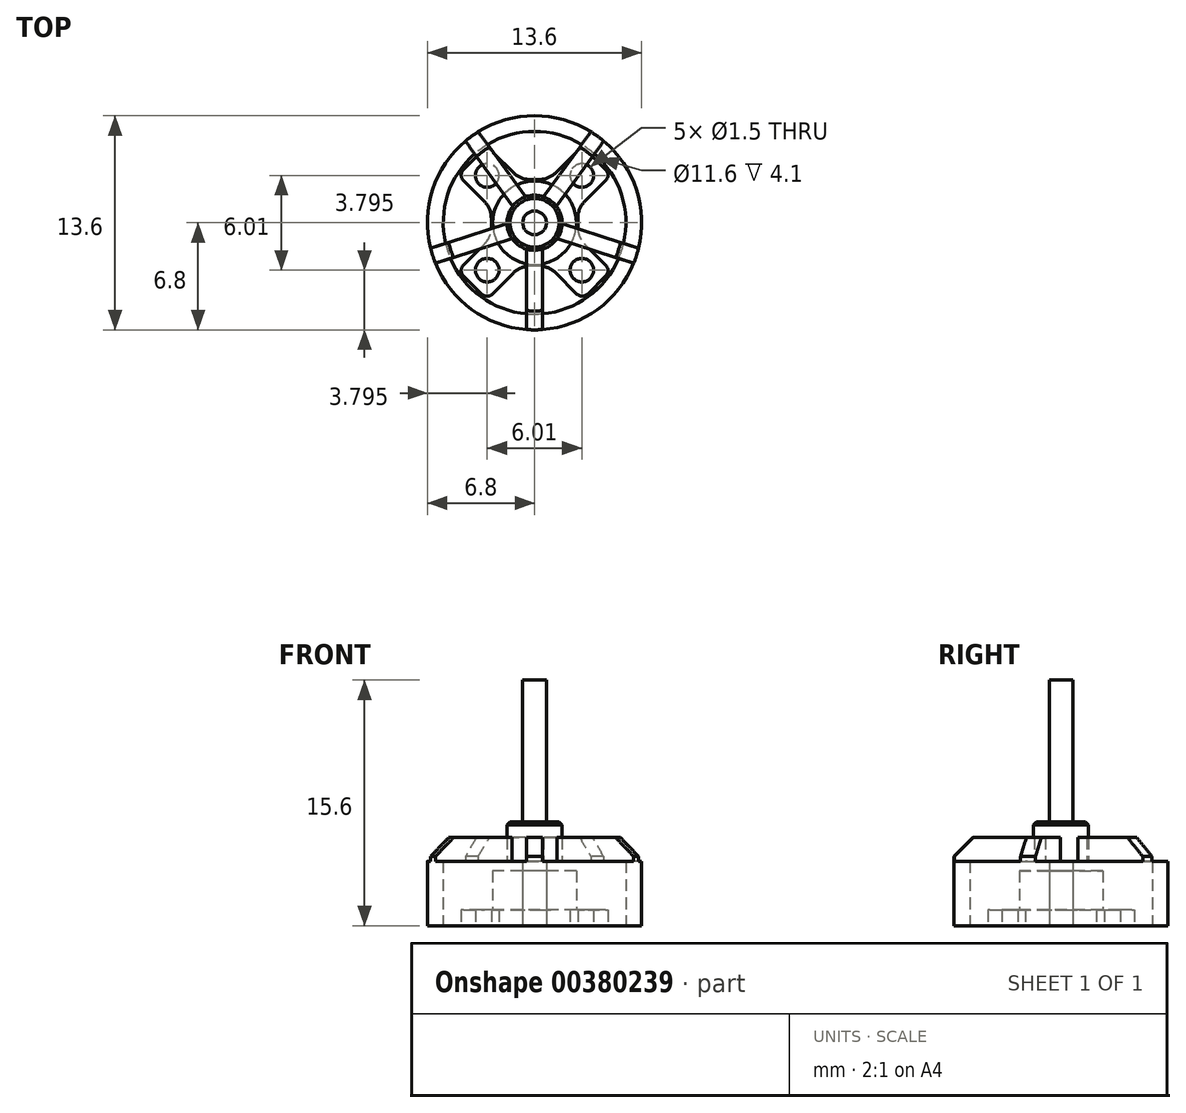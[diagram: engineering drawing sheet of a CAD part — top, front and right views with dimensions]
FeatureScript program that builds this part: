
annotation { "Feature Type Name" : "Feature", "Feature Type Description" : "" }
export const myFeature = defineFeature(function(context is Context, id is Id, definition is map)
    precondition{}
    {
        {
            var Q0;
            Q0=qCreatedBy(makeId("Top.planeOp"),FACE);
            var sketch = newSketch(context, id + "F0", { "sketchPlane" : qUnion([Q0])});
            skCircle(sketch, "E0", {"center": v(0, 0) * mm, "radius": 4.25 * mm, "construction": true});
            skLineSegment(sketch, "E1", {"start": v(-7.64, 0) * mm, "end": v(7.53, 0) * mm, "construction": true});
            skLineSegment(sketch, "E2", {"start": v(0, 0) * mm, "end": v(-7.7, 7.7) * mm, "construction": true});
            skLineSegment(sketch, "E3", {"start": v(0, 0) * mm, "end": v(5.02, -5.02) * mm, "construction": true});
            skLineSegment(sketch, "E4", {"start": v(0, 0) * mm, "end": v(-5.33, -5.33) * mm, "construction": true});
            skLineSegment(sketch, "E5", {"start": v(0, 0) * mm, "end": v(4.89, 4.89) * mm, "construction": true});
            skCircle(sketch, "E6", {"center": v(-3, 3) * mm, "radius": 0.75 * mm});
            skCircle(sketch, "E7", {"center": v(3, 3) * mm, "radius": 0.75 * mm});
            skCircle(sketch, "E8", {"center": v(3, -3) * mm, "radius": 0.75 * mm});
            skCircle(sketch, "E9", {"center": v(-3, -3) * mm, "radius": 0.75 * mm});
            skLineSegment(sketch, "E10", {"start": v(3.38, 4.51) * mm, "end": v(4.51, 3.38) * mm});
            skCircle(sketch, "E11", {"center": v(0, 0) * mm, "radius": 1.74 * mm, "construction": true});
            skLineSegment(sketch, "E12", {"start": v(2.68, 4.51) * mm, "end": v(1.35, 3.19) * mm});
            skLineSegment(sketch, "E13", {"start": v(4.51, 2.68) * mm, "end": v(3.19, 1.35) * mm});
            skPoint(sketch, "E14.visualSharp", {"position": v(3.03, 4.87) * mm});
            skArc(sketch, "E14.filletArc", {"start": v(3.38, 4.51) * mm, "mid": v(3.03, 4.66) * mm, "end": v(2.68, 4.51) * mm});
            skPoint(sketch, "E15.visualSharp", {"position": v(4.87, 3.03) * mm});
            skArc(sketch, "E15.filletArc", {"start": v(4.51, 2.68) * mm, "mid": v(4.66, 3.03) * mm, "end": v(4.51, 3.38) * mm});
            skLineSegment(sketch, "E16", {"start": v(0, 5.01) * mm, "end": v(0, -5.05) * mm, "construction": true});
            skLineSegment(sketch, "E17.MirrorCS", {"start": v(-2.68, 4.51) * mm, "end": v(-1.35, 3.19) * mm});
            skArc(sketch, "E18.MirrorCS", {"start": v(-3.38, 4.51) * mm, "mid": v(-3.03, 4.66) * mm, "end": v(-2.68, 4.51) * mm});
            skLineSegment(sketch, "E19.MirrorCS", {"start": v(-3.38, 4.51) * mm, "end": v(-4.51, 3.38) * mm});
            skLineSegment(sketch, "E20.MirrorCS", {"start": v(-4.51, 2.68) * mm, "end": v(-3.19, 1.35) * mm});
            skArc(sketch, "E21.MirrorCS", {"start": v(-4.51, 2.68) * mm, "mid": v(-4.66, 3.03) * mm, "end": v(-4.51, 3.38) * mm});
            skLineSegment(sketch, "E22.MirrorCS", {"start": v(-4.51, -2.68) * mm, "end": v(-3.19, -1.35) * mm});
            skArc(sketch, "E23.MirrorCS", {"start": v(-4.51, -2.68) * mm, "mid": v(-4.66, -3.03) * mm, "end": v(-4.51, -3.38) * mm});
            skLineSegment(sketch, "E24.MirrorCS", {"start": v(-3.38, -4.51) * mm, "end": v(-4.51, -3.38) * mm});
            skArc(sketch, "E25.MirrorCS", {"start": v(-3.38, -4.51) * mm, "mid": v(-3.03, -4.66) * mm, "end": v(-2.68, -4.51) * mm});
            skLineSegment(sketch, "E26.MirrorCS", {"start": v(-2.68, -4.51) * mm, "end": v(-1.35, -3.19) * mm});
            skLineSegment(sketch, "E27.MirrorCS", {"start": v(2.68, -4.51) * mm, "end": v(1.35, -3.19) * mm});
            skArc(sketch, "E28.MirrorCS", {"start": v(3.38, -4.51) * mm, "mid": v(3.03, -4.66) * mm, "end": v(2.68, -4.51) * mm});
            skLineSegment(sketch, "E29.MirrorCS", {"start": v(3.38, -4.51) * mm, "end": v(4.51, -3.38) * mm});
            skArc(sketch, "E30.MirrorCS", {"start": v(4.51, -2.68) * mm, "mid": v(4.66, -3.03) * mm, "end": v(4.51, -3.38) * mm});
            skLineSegment(sketch, "E31.MirrorCS", {"start": v(4.51, -2.68) * mm, "end": v(3.19, -1.35) * mm});
            skLineSegment(sketch, "E32", {"start": v(-0.29, 2.75) * mm, "end": v(0.29, 2.75) * mm});
            skLineSegment(sketch, "E33", {"start": v(2.75, 0.29) * mm, "end": v(2.75, -0.29) * mm});
            skLineSegment(sketch, "E34", {"start": v(0.29, -2.75) * mm, "end": v(-0.29, -2.75) * mm});
            skLineSegment(sketch, "E35", {"start": v(-2.75, -0.29) * mm, "end": v(-2.75, 0.29) * mm});
            skPoint(sketch, "E36.visualSharp", {"position": v(-0.9, 2.75) * mm});
            skArc(sketch, "E36.filletArc", {"start": v(-1.35, 3.19) * mm, "mid": v(-0.86, 2.86) * mm, "end": v(-0.29, 2.75) * mm});
            skPoint(sketch, "E37.visualSharp", {"position": v(0.9, 2.75) * mm});
            skArc(sketch, "E37.filletArc", {"start": v(0.29, 2.75) * mm, "mid": v(0.86, 2.86) * mm, "end": v(1.35, 3.19) * mm});
            skPoint(sketch, "E38.visualSharp", {"position": v(-2.75, -0.9) * mm});
            skArc(sketch, "E38.filletArc", {"start": v(-3.19, -1.35) * mm, "mid": v(-2.86, -0.86) * mm, "end": v(-2.75, -0.29) * mm});
            skPoint(sketch, "E39.visualSharp", {"position": v(-2.75, 0.9) * mm});
            skArc(sketch, "E39.filletArc", {"start": v(-2.75, 0.29) * mm, "mid": v(-2.86, 0.86) * mm, "end": v(-3.19, 1.35) * mm});
            skPoint(sketch, "E40.visualSharp", {"position": v(2.75, 0.9) * mm});
            skArc(sketch, "E40.filletArc", {"start": v(3.19, 1.35) * mm, "mid": v(2.86, 0.86) * mm, "end": v(2.75, 0.29) * mm});
            skPoint(sketch, "E41.visualSharp", {"position": v(2.75, -0.9) * mm});
            skArc(sketch, "E41.filletArc", {"start": v(2.75, -0.29) * mm, "mid": v(2.86, -0.86) * mm, "end": v(3.19, -1.35) * mm});
            skPoint(sketch, "E42.visualSharp", {"position": v(0.9, -2.75) * mm});
            skArc(sketch, "E42.filletArc", {"start": v(1.35, -3.19) * mm, "mid": v(0.86, -2.86) * mm, "end": v(0.29, -2.75) * mm});
            skPoint(sketch, "E43.visualSharp", {"position": v(-0.9, -2.75) * mm});
            skArc(sketch, "E43.filletArc", {"start": v(-0.29, -2.75) * mm, "mid": v(-0.86, -2.86) * mm, "end": v(-1.35, -3.19) * mm});
            skCircle(sketch, "E44", {"center": v(0, 0) * mm, "radius": 0.75 * mm});
            skSolve(sketch);
        }
        {
            var Q0;
            Q0=makeQuery(id+"F0.imprint","IMPRINT",FACE,{"disambiguationData":[TD([[makeQuery(id+"F0.imprint","IMPRINT",EDGE,{"derivedFrom":sQuery(id+"F0.wireOp",EDGE,"E6")}),-1.0]])]});
            extrude(context, id + "F1", {"entities" : qUnion([Q0]), "depth" : 1 * mm});
        }
        {
            var Q0;
            Q0=qCreatedBy(makeId("Top.planeOp"),FACE);
            var sketch = newSketch(context, id + "F2", { "sketchPlane" : qUnion([Q0])});
            skCircle(sketch, "E45", {"center": v(0, 0) * mm, "radius": 6.8 * mm});
            skCircle(sketch, "E46", {"center": v(0, 0) * mm, "radius": 5.8 * mm});
            skSolve(sketch);
        }
        {
            var Q0;
            Q0=makeQuery(id+"F2.imprint","IMPRINT",FACE,{"disambiguationData":[TD([[makeQuery(id+"F2.imprint","IMPRINT",EDGE,{"derivedFrom":sQuery(id+"F2.wireOp",EDGE,"E45")}),1.0]])]});
            extrude(context, id + "F3", {"entities" : qUnion([Q0]), "depth" : 4.1 * mm});
        }
        {
            var Q0;
            Q0=makeQuery(id+"F1.opExtrude","CAP_FACE",FACE,{"disambiguationData":[OSD([sQuery(id+"F0.wireOp",EDGE,"E6"),sQuery(id+"F0.wireOp",EDGE,"E7"),sQuery(id+"F0.wireOp",EDGE,"E8"),sQuery(id+"F0.wireOp",EDGE,"E9"),sQuery(id+"F0.wireOp",EDGE,"E10"),sQuery(id+"F0.wireOp",EDGE,"E12"),sQuery(id+"F0.wireOp",EDGE,"E13"),sQuery(id+"F0.wireOp",EDGE,"E14.filletArc"),sQuery(id+"F0.wireOp",EDGE,"E15.filletArc"),sQuery(id+"F0.wireOp",EDGE,"E17.MirrorCS"),sQuery(id+"F0.wireOp",EDGE,"E18.MirrorCS"),sQuery(id+"F0.wireOp",EDGE,"E19.MirrorCS"),sQuery(id+"F0.wireOp",EDGE,"E20.MirrorCS"),sQuery(id+"F0.wireOp",EDGE,"E21.MirrorCS"),sQuery(id+"F0.wireOp",EDGE,"E22.MirrorCS"),sQuery(id+"F0.wireOp",EDGE,"E23.MirrorCS"),sQuery(id+"F0.wireOp",EDGE,"E24.MirrorCS"),sQuery(id+"F0.wireOp",EDGE,"E25.MirrorCS"),sQuery(id+"F0.wireOp",EDGE,"E26.MirrorCS"),sQuery(id+"F0.wireOp",EDGE,"E27.MirrorCS"),sQuery(id+"F0.wireOp",EDGE,"E28.MirrorCS"),sQuery(id+"F0.wireOp",EDGE,"E29.MirrorCS"),sQuery(id+"F0.wireOp",EDGE,"E30.MirrorCS"),sQuery(id+"F0.wireOp",EDGE,"E31.MirrorCS"),sQuery(id+"F0.wireOp",EDGE,"E32"),sQuery(id+"F0.wireOp",EDGE,"E33"),sQuery(id+"F0.wireOp",EDGE,"E34"),sQuery(id+"F0.wireOp",EDGE,"E35"),sQuery(id+"F0.wireOp",EDGE,"E36.filletArc"),sQuery(id+"F0.wireOp",EDGE,"E37.filletArc"),sQuery(id+"F0.wireOp",EDGE,"E38.filletArc"),sQuery(id+"F0.wireOp",EDGE,"E39.filletArc"),sQuery(id+"F0.wireOp",EDGE,"E40.filletArc"),sQuery(id+"F0.wireOp",EDGE,"E41.filletArc"),sQuery(id+"F0.wireOp",EDGE,"E42.filletArc"),sQuery(id+"F0.wireOp",EDGE,"E43.filletArc")])],"isStart":false});
            var sketch = newSketch(context, id + "F4", { "sketchPlane" : qUnion([Q0])});
            skCircle(sketch, "E47", {"center": v(0, 0) * mm, "radius": 2.66 * mm});
            skSolve(sketch);
        }
        {
            var Q0;
            Q0=makeQuery(id+"F4.imprint","IMPRINT",FACE,{"disambiguationData":[TD([[makeQuery(id+"F4.imprint","IMPRINT",EDGE,{"derivedFrom":sQuery(id+"F4.wireOp",EDGE,"E47")}),1.0]])]});
            extrude(context, id + "F5", {"entities" : qUnion([Q0]), "operationType" : NewBodyOperationType.ADD, "depth" : 2.5 * mm});
        }
        {
            var Q0;
            Q0=makeQuery(id+"F3.opExtrude","CAP_FACE",FACE,{"disambiguationData":[OSD([sQuery(id+"F2.wireOp",EDGE,"E45"),sQuery(id+"F2.wireOp",EDGE,"E46")])],"isStart":false});
            var sketch = newSketch(context, id + "F6", { "sketchPlane" : qUnion([Q0])});
            skLineSegment(sketch, "E48", {"start": v(0, -8.68) * mm, "end": v(0, 0) * mm, "construction": true});
            skLineSegment(sketch, "E49", {"start": v(0, 0) * mm, "end": v(-6.56, 9.02) * mm, "construction": true});
            skLineSegment(sketch, "E50", {"start": v(0, 0) * mm, "end": v(5.24, 7.22) * mm, "construction": true});
            skLineSegment(sketch, "E51", {"start": v(0, 0) * mm, "end": v(8.23, -2.67) * mm, "construction": true});
            skCircle(sketch, "E52", {"center": v(0, 0) * mm, "radius": 1.75 * mm});
            skCircle(sketch, "E53", {"center": v(0, 0) * mm, "radius": 0.75 * mm});
            skLineSegment(sketch, "E54", {"start": v(-1.66, -0.54) * mm, "end": v(-6.47, -2.1) * mm, "construction": true});
            skLineSegment(sketch, "E55", {"start": v(-4.07, -1.32) * mm, "end": v(-4.22, -0.85) * mm, "construction": true});
            skLineSegment(sketch, "E56", {"start": v(-4.22, -0.85) * mm, "end": v(-6.6, -1.62) * mm});
            skLineSegment(sketch, "E57", {"start": v(-4.22, -0.85) * mm, "end": v(-1.75, -0.04) * mm});
            skLineSegment(sketch, "E58", {"start": v(-4.07, -1.32) * mm, "end": v(-3.91, -1.8) * mm, "construction": true});
            skLineSegment(sketch, "E59", {"start": v(-3.91, -1.8) * mm, "end": v(-6.3, -2.57) * mm});
            skLineSegment(sketch, "E60", {"start": v(-3.91, -1.8) * mm, "end": v(-1.44, -1) * mm});
            skLineSegment(sketch, "E61.1.0", {"start": v(-0.5, -4.27) * mm, "end": v(-0.5, -6.78) * mm});
            skLineSegment(sketch, "E61.1.1", {"start": v(-0.5, -4.27) * mm, "end": v(-0.5, -1.68) * mm});
            skLineSegment(sketch, "E61.1.2", {"start": v(0.5, -4.28) * mm, "end": v(0.5, -1.68) * mm});
            skLineSegment(sketch, "E61.1.3", {"start": v(0.5, -4.27) * mm, "end": v(0.5, -6.78) * mm});
            skLineSegment(sketch, "E61.2.0", {"start": v(3.91, -1.8) * mm, "end": v(6.3, -2.57) * mm});
            skLineSegment(sketch, "E61.2.1", {"start": v(3.91, -1.8) * mm, "end": v(1.44, -1) * mm});
            skLineSegment(sketch, "E61.2.2", {"start": v(4.22, -0.85) * mm, "end": v(1.75, -0.04) * mm});
            skLineSegment(sketch, "E61.2.3", {"start": v(4.22, -0.85) * mm, "end": v(6.6, -1.62) * mm});
            skLineSegment(sketch, "E61.3.0", {"start": v(2.92, 3.16) * mm, "end": v(4.4, 5.2) * mm});
            skLineSegment(sketch, "E61.3.1", {"start": v(2.92, 3.16) * mm, "end": v(1.4, 1.06) * mm});
            skLineSegment(sketch, "E61.3.2", {"start": v(2.1, 3.75) * mm, "end": v(0.58, 1.65) * mm});
            skLineSegment(sketch, "E61.3.3", {"start": v(2.1, 3.75) * mm, "end": v(3.58, 5.78) * mm});
            skLineSegment(sketch, "E61.4.0", {"start": v(-2.1, 3.75) * mm, "end": v(-3.58, 5.78) * mm});
            skLineSegment(sketch, "E61.4.1", {"start": v(-2.1, 3.75) * mm, "end": v(-0.58, 1.65) * mm});
            skLineSegment(sketch, "E61.4.2", {"start": v(-2.92, 3.16) * mm, "end": v(-1.4, 1.06) * mm});
            skLineSegment(sketch, "E61.4.3", {"start": v(-2.92, 3.16) * mm, "end": v(-4.4, 5.2) * mm});
            skSolve(sketch);
        }
        {
            var Q0;
            {var subQ6=sQuery(id+"F6.wireOp",EDGE,"E61.4.1");Q0=makeQuery(id+"F6.imprint","IMPRINT",FACE,{"disambiguationData":[TD([[makeQuery(id+"F6.imprint","IMPRINT",EDGE,{"derivedFrom":subQ6}),-1.0]])]});}
            var Q1;
            {var subQ0=sQuery(id+"F6.wireOp",EDGE,"E61.4.0");var subQ1=makeQuery(id+"F3.opExtrude","CAP_EDGE",EDGE,{"disambiguationData":[OSD([sQuery(id+"F2.wireOp",EDGE,"E45")])],"isStart":false});var subQ2=makeQuery(id+"F6.imprint","INTERSECT",VERTEX,{"derivedFrom":[subQ1,subQ0]});Q1=makeQuery(id+"F6.imprint","IMPRINT",FACE,{"disambiguationData":[TD([[makeQuery(id+"F6.imprint","IMPRINT",EDGE,{"disambiguationData":[TD([[subQ2,1.0]])],"derivedFrom":subQ0}),1.0]])]});}
            var Q2;
            {var subQ1=sQuery(id+"F6.wireOp",EDGE,"E61.3.1");Q2=makeQuery(id+"F6.imprint","IMPRINT",FACE,{"disambiguationData":[TD([[makeQuery(id+"F6.imprint","IMPRINT",EDGE,{"derivedFrom":subQ1}),-1.0]])]});}
            var Q3;
            {var subQ0=sQuery(id+"F6.wireOp",EDGE,"E61.3.0");var subQ1=makeQuery(id+"F3.opExtrude","CAP_EDGE",EDGE,{"disambiguationData":[OSD([sQuery(id+"F2.wireOp",EDGE,"E45")])],"isStart":false});var subQ2=makeQuery(id+"F6.imprint","INTERSECT",VERTEX,{"derivedFrom":[subQ1,subQ0]});Q3=makeQuery(id+"F6.imprint","IMPRINT",FACE,{"disambiguationData":[TD([[makeQuery(id+"F6.imprint","IMPRINT",EDGE,{"disambiguationData":[TD([[subQ2,1.0]])],"derivedFrom":subQ0}),1.0]])]});}
            var Q4;
            {var subQ1=sQuery(id+"F6.wireOp",EDGE,"E61.2.1");Q4=makeQuery(id+"F6.imprint","IMPRINT",FACE,{"disambiguationData":[TD([[makeQuery(id+"F6.imprint","IMPRINT",EDGE,{"derivedFrom":subQ1}),-1.0]])]});}
            var Q5;
            {var subQ0=sQuery(id+"F6.wireOp",EDGE,"E61.2.0");var subQ1=makeQuery(id+"F3.opExtrude","CAP_EDGE",EDGE,{"disambiguationData":[OSD([sQuery(id+"F2.wireOp",EDGE,"E45")])],"isStart":false});var subQ2=makeQuery(id+"F6.imprint","INTERSECT",VERTEX,{"derivedFrom":[subQ1,subQ0]});Q5=makeQuery(id+"F6.imprint","IMPRINT",FACE,{"disambiguationData":[TD([[makeQuery(id+"F6.imprint","IMPRINT",EDGE,{"disambiguationData":[TD([[subQ2,1.0]])],"derivedFrom":subQ0}),1.0]])]});}
            var Q6;
            {var subQ1=sQuery(id+"F6.wireOp",EDGE,"E61.1.1");Q6=makeQuery(id+"F6.imprint","IMPRINT",FACE,{"disambiguationData":[TD([[makeQuery(id+"F6.imprint","IMPRINT",EDGE,{"derivedFrom":subQ1}),-1.0]])]});}
            var Q7;
            {var subQ0=sQuery(id+"F6.wireOp",EDGE,"E57");Q7=makeQuery(id+"F6.imprint","IMPRINT",FACE,{"disambiguationData":[TD([[makeQuery(id+"F6.imprint","IMPRINT",EDGE,{"derivedFrom":subQ0}),-1.0]])]});}
            var Q8;
            {var subQ0=sQuery(id+"F6.wireOp",EDGE,"E56");var subQ1=makeQuery(id+"F3.opExtrude","CAP_EDGE",EDGE,{"disambiguationData":[OSD([sQuery(id+"F2.wireOp",EDGE,"E45")])],"isStart":false});var subQ2=makeQuery(id+"F6.imprint","INTERSECT",VERTEX,{"derivedFrom":[subQ1,subQ0]});Q8=makeQuery(id+"F6.imprint","IMPRINT",FACE,{"disambiguationData":[TD([[makeQuery(id+"F6.imprint","IMPRINT",EDGE,{"disambiguationData":[TD([[subQ2,1.0]])],"derivedFrom":subQ0}),1.0]])]});}
            var Q9;
            Q9=makeQuery(id+"F6.imprint","IMPRINT",FACE,{"disambiguationData":[TD([[makeQuery(id+"F6.imprint","IMPRINT",EDGE,{"derivedFrom":sQuery(id+"F6.wireOp",EDGE,"E53")}),-1.0]])]});
            var Q10;
            {var subQ0=sQuery(id+"F6.wireOp",EDGE,"E61.1.0");var subQ1=makeQuery(id+"F3.opExtrude","CAP_EDGE",EDGE,{"disambiguationData":[OSD([sQuery(id+"F2.wireOp",EDGE,"E45")])],"isStart":false});var subQ2=makeQuery(id+"F6.imprint","INTERSECT",VERTEX,{"derivedFrom":[subQ1,subQ0]});Q10=makeQuery(id+"F6.imprint","IMPRINT",FACE,{"disambiguationData":[TD([[makeQuery(id+"F6.imprint","IMPRINT",EDGE,{"disambiguationData":[TD([[subQ2,1.0]])],"derivedFrom":subQ0}),1.0]])]});}
            extrude(context, id + "F7", {"entities" : qUnion([Q0, Q1, Q2, Q3, Q4, Q5, Q6, Q7, Q8, Q9, Q10]), "operationType" : NewBodyOperationType.ADD, "depth" : 1.5 * mm});
        }
        {
            var Q0;
            {var subQ0=sQuery(id+"F2.wireOp",EDGE,"E45");var subQ1=makeQuery(id+"F3.opExtrude","CAP_EDGE",EDGE,{"disambiguationData":[OSD([subQ0])],"isStart":false});Q0=makeQuery(id+"F7.opExtrude","CAP_EDGE",EDGE,{"disambiguationData":[OSD([subQ0]),TDD([makeQuery(id+"F6.imprint","IMPRINT",EDGE,{"disambiguationData":[TD([[makeQuery(id+"F6.imprint","INTERSECT",VERTEX,{"derivedFrom":[subQ1,sQuery(id+"F6.wireOp",EDGE,"E56")]}),-1.0]])],"derivedFrom":subQ1})])],"isStart":false});}
            var Q1;
            {var subQ0=sQuery(id+"F2.wireOp",EDGE,"E45");var subQ1=makeQuery(id+"F3.opExtrude","CAP_EDGE",EDGE,{"disambiguationData":[OSD([subQ0])],"isStart":false});Q1=makeQuery(id+"F7.opExtrude","CAP_EDGE",EDGE,{"disambiguationData":[OSD([subQ0]),TDD([makeQuery(id+"F6.imprint","IMPRINT",EDGE,{"disambiguationData":[TD([[makeQuery(id+"F6.imprint","INTERSECT",VERTEX,{"derivedFrom":[subQ1,sQuery(id+"F6.wireOp",EDGE,"E61.4.0")]}),-1.0]])],"derivedFrom":subQ1})])],"isStart":false});}
            var Q2;
            {var subQ0=sQuery(id+"F2.wireOp",EDGE,"E45");var subQ1=makeQuery(id+"F3.opExtrude","CAP_EDGE",EDGE,{"disambiguationData":[OSD([subQ0])],"isStart":false});Q2=makeQuery(id+"F7.opExtrude","CAP_EDGE",EDGE,{"disambiguationData":[OSD([subQ0]),TDD([makeQuery(id+"F6.imprint","IMPRINT",EDGE,{"disambiguationData":[TD([[makeQuery(id+"F6.imprint","INTERSECT",VERTEX,{"derivedFrom":[subQ1,sQuery(id+"F6.wireOp",EDGE,"E61.3.0")]}),-1.0]])],"derivedFrom":subQ1})])],"isStart":false});}
            var Q3;
            {var subQ0=sQuery(id+"F2.wireOp",EDGE,"E45");var subQ1=makeQuery(id+"F3.opExtrude","CAP_EDGE",EDGE,{"disambiguationData":[OSD([subQ0])],"isStart":false});Q3=makeQuery(id+"F7.opExtrude","CAP_EDGE",EDGE,{"disambiguationData":[OSD([subQ0]),TDD([makeQuery(id+"F6.imprint","IMPRINT",EDGE,{"disambiguationData":[TD([[makeQuery(id+"F6.imprint","INTERSECT",VERTEX,{"derivedFrom":[subQ1,sQuery(id+"F6.wireOp",EDGE,"E61.2.0")]}),-1.0]])],"derivedFrom":subQ1})])],"isStart":false});}
            var Q4;
            {var subQ0=sQuery(id+"F2.wireOp",EDGE,"E45");var subQ1=makeQuery(id+"F3.opExtrude","CAP_EDGE",EDGE,{"disambiguationData":[OSD([subQ0])],"isStart":false});Q4=makeQuery(id+"F7.opExtrude","CAP_EDGE",EDGE,{"disambiguationData":[OSD([subQ0]),TDD([makeQuery(id+"F6.imprint","IMPRINT",EDGE,{"disambiguationData":[TD([[makeQuery(id+"F6.imprint","INTERSECT",VERTEX,{"derivedFrom":[subQ1,sQuery(id+"F6.wireOp",EDGE,"E61.1.0")]}),-1.0]])],"derivedFrom":subQ1})])],"isStart":false});}
            chamfer(context, id + "F8", {"entities" : qUnion([Q0, Q1, Q2, Q3, Q4]), "width" : 1.2 * mm, "tangentPropagation" : true});
        }
        {
            var Q0;
            Q0=qCreatedBy(makeId("Top.planeOp"),FACE);
            var sketch = newSketch(context, id + "F9", { "sketchPlane" : qUnion([Q0])});
            skCircle(sketch, "E62", {"center": v(0, 0) * mm, "radius": 0.75 * mm});
            skSolve(sketch);
        }
        {
            var Q0;
            Q0=makeQuery(id+"F9.imprint","IMPRINT",FACE,{"disambiguationData":[TD([[makeQuery(id+"F9.imprint","IMPRINT",EDGE,{"derivedFrom":sQuery(id+"F9.wireOp",EDGE,"E62")}),1.0]])]});
            extrude(context, id + "F10", {"entities" : qUnion([Q0]), "depth" : 15.6 * mm});
        }
        {
            var Q0;
            Q0=makeQuery(id+"F7.opExtrude","CAP_FACE",FACE,{"disambiguationData":[OSD([sQuery(id+"F2.wireOp",EDGE,"E45"),sQuery(id+"F6.wireOp",EDGE,"E52"),sQuery(id+"F6.wireOp",EDGE,"E53"),sQuery(id+"F6.wireOp",EDGE,"E56"),sQuery(id+"F6.wireOp",EDGE,"E57"),sQuery(id+"F6.wireOp",EDGE,"E59"),sQuery(id+"F6.wireOp",EDGE,"E60"),sQuery(id+"F6.wireOp",EDGE,"E61.1.0"),sQuery(id+"F6.wireOp",EDGE,"E61.1.1"),sQuery(id+"F6.wireOp",EDGE,"E61.1.2"),sQuery(id+"F6.wireOp",EDGE,"E61.1.3"),sQuery(id+"F6.wireOp",EDGE,"E61.2.0"),sQuery(id+"F6.wireOp",EDGE,"E61.2.1"),sQuery(id+"F6.wireOp",EDGE,"E61.2.2"),sQuery(id+"F6.wireOp",EDGE,"E61.2.3"),sQuery(id+"F6.wireOp",EDGE,"E61.3.0"),sQuery(id+"F6.wireOp",EDGE,"E61.3.1"),sQuery(id+"F6.wireOp",EDGE,"E61.3.2"),sQuery(id+"F6.wireOp",EDGE,"E61.3.3"),sQuery(id+"F6.wireOp",EDGE,"E61.4.0"),sQuery(id+"F6.wireOp",EDGE,"E61.4.1"),sQuery(id+"F6.wireOp",EDGE,"E61.4.2"),sQuery(id+"F6.wireOp",EDGE,"E61.4.3")])],"isStart":false});
            var sketch = newSketch(context, id + "F11", { "sketchPlane" : qUnion([Q0])});
            skCircle(sketch, "E63", {"center": v(0, 0) * mm, "radius": 1.75 * mm});
            skSolve(sketch);
        }
        {
            var Q0;
            Q0=makeQuery(id+"F11.imprint","IMPRINT",FACE,{"disambiguationData":[TD([[makeQuery(id+"F11.imprint","IMPRINT",EDGE,{"derivedFrom":makeQuery(id+"F7.opExtrude","CAP_EDGE",EDGE,{"disambiguationData":[OSD([sQuery(id+"F6.wireOp",EDGE,"E53")])],"isStart":false})}),-1.0]])]});
            extrude(context, id + "F12", {"entities" : qUnion([Q0]), "operationType" : NewBodyOperationType.ADD, "depth" : 1 * mm});
        }
        {
            var Q0;
            Q0=makeQuery(id+"F12.opExtrude","CAP_EDGE",EDGE,{"disambiguationData":[OSD([sQuery(id+"F11.wireOp",EDGE,"E63")])],"isStart":false});
            chamfer(context, id + "F13", {"entities" : qUnion([Q0]), "width" : 0.2 * mm, "tangentPropagation" : true});
        }
    });
